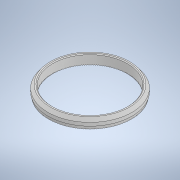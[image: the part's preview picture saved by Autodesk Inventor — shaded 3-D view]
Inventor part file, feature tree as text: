
AUTODESK INVENTOR PART (.ipt)
format: ipt  version: 2020.5 (Build 245400000, 400)  size: 627,712 bytes
history: native  units: mm
features: chamfer x3, extrude x2, sketch x2, pattern_circular x1
ambient origin geometry x8: Origin, YZ Plane, XZ Plane, XY Plane, X Axis, Y Axis, Z Axis, Center Point
bodies: Solid1 (feature_tree)
feature tree (8):
  extrude  "Extrusion1"  Depth=3.0mm
  chamfer  "Chamfer1"  Distance=3.0mm
  chamfer  "Chamfer2"  Distance=0.25mm Angle=45.0deg
  chamfer  "Chamfer3"  Distance=1.0mm Angle=45.0deg
  extrude  "Extrusion3"  Depth=0.5mm
  pattern_circular  "Circular Pattern2"  Count=180 Angle=360.0deg
  sketch  "Sketch1"  dims[d0=22.7mm d1=25.5mm d2=3.0mm d3=0.0mm d4=0.25mm d5=1.0mm d6=45.0deg d7=1.0mm d8=0.25mm d9=45.0deg]
  sketch  "Sketch5"  dims[d10=0.75mm d11=1.0mm d12=45.0deg d23=0.2mm d24=-7.853982mm d25=1800.0mm d26=360.0deg d13=0.5mm d14=0.872665mm d15=0.5mm d16=0.872665mm d17=0.872665mm d18=0.5mm d19=0.872665mm]
